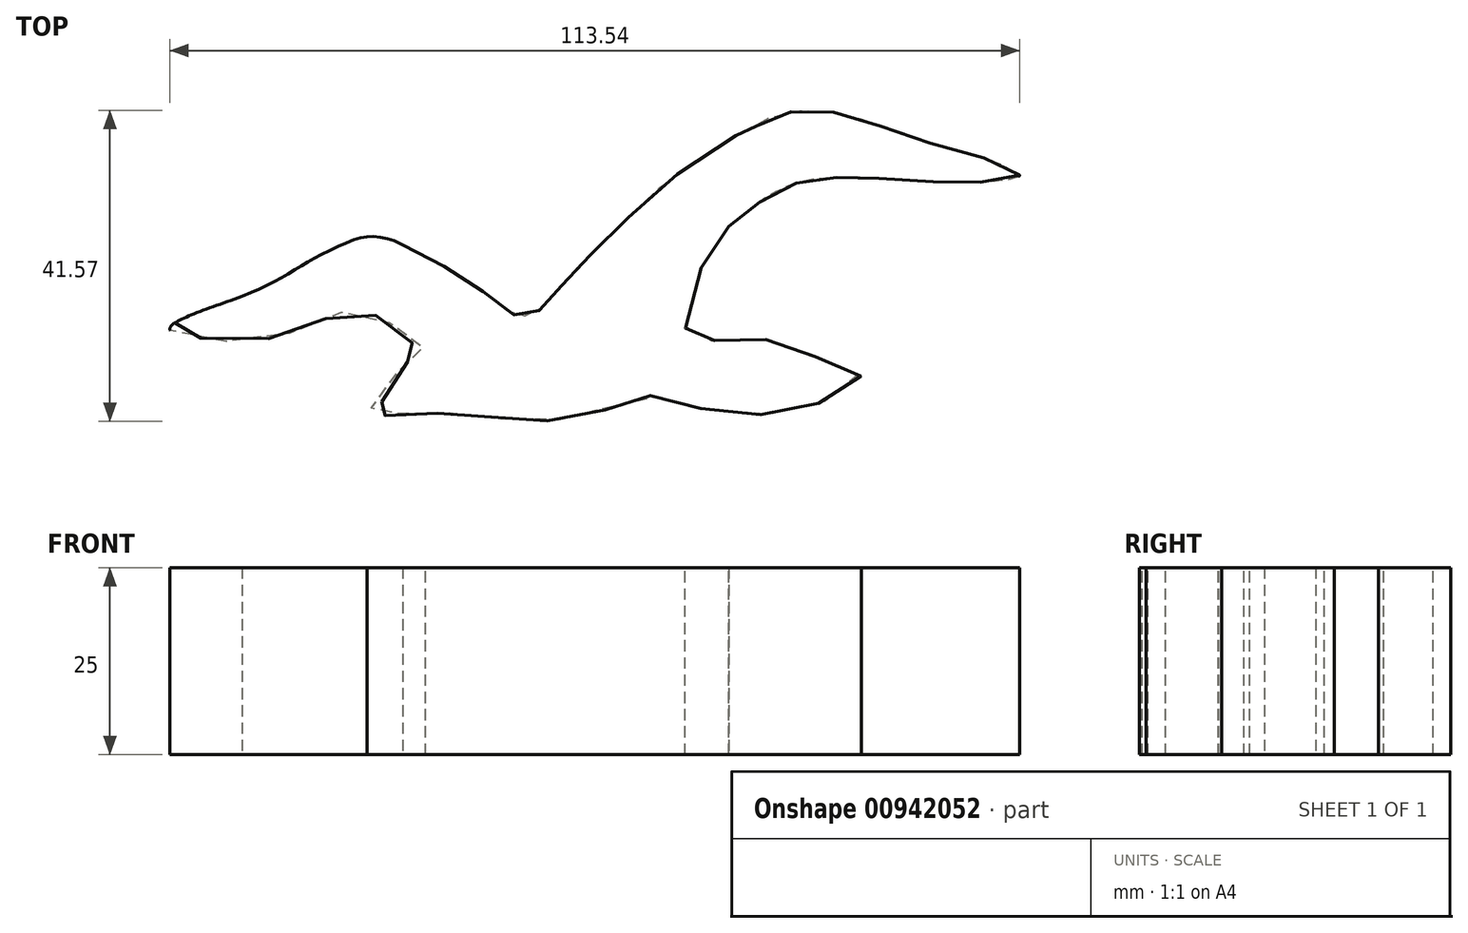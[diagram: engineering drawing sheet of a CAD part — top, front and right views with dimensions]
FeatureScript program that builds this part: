
annotation { "Feature Type Name" : "Feature", "Feature Type Description" : "" }
export const myFeature = defineFeature(function(context is Context, id is Id, definition is map)
    precondition{}
    {
        {
            var Q0;
            Q0=qCreatedBy(makeId("Top.planeOp"),FACE);
            var sketch = newSketch(context, id + "F0", { "sketchPlane" : qUnion([Q0])});
            skFitSpline(sketch, "E0", {"points": [v(-56.8, -12.41) * mm, v(-47.84, -8.9) * mm, v(-43.6, -6.97) * mm, v(-40.35, -5.11) * mm, v(-37.37, -3.4) * mm, v(-33.09, -1.42) * mm, v(-30.48, -0.9) * mm, v(-27.61, -1.42) * mm, v(-26.38, -2.02) * mm, v(-26.53, -2.1) * mm], "startDerivative": vector(50.93, 19.5) * mm, "endDerivative": vector(-17.67, -8.84) * mm});
            skFitSpline(sketch, "E1", {"points": [v(-26.38, -2.02) * mm, v(-21.97, -4.25) * mm, v(-16.88, -7.33) * mm, v(-14.1, -9.41) * mm, v(-11.23, -11.5) * mm, v(-10.2, -11.54) * mm, v(-8.2, -10.8) * mm, v(-6.98, -9.57) * mm, v(-4.36, -6.6) * mm, v(-1.68, -3.75) * mm, v(3.01, 0.89) * mm, v(10.34, 7.48) * mm, v(18.94, 13.1) * mm, v(19.68, 13.64) * mm, v(20.46, 13.64) * mm, v(22.1, 14.7) * mm, v(26.24, 15.86) * mm, v(30.42, 15.78) * mm, v(35.71, 14.5) * mm, v(41.56, 12.28) * mm, v(48.73, 10.37) * mm, v(54.54, 8.34) * mm, v(56.05, 7.23) * mm, v(52.6, 6.47) * mm, v(47.46, 6.35) * mm, v(40.93, 6.63) * mm, v(34.66, 6.98) * mm, v(31.1, 6.94) * mm, v(27.22, 6.47) * mm, v(23.1, 4.87) * mm, v(20.2, 2.8) * mm, v(17.19, 0.44) * mm], "startDerivative": vector(119.97, -57.7) * mm, "endDerivative": vector(-98.87, -76.43) * mm});
            skFitSpline(sketch, "E2", {"points": [v(17.19, 0.44) * mm, v(17.19, 0) * mm, v(15.2, -2.55) * mm, v(12.63, -6.86) * mm, v(11.41, -11.72) * mm, v(11.58, -14.81) * mm, v(11.74, -15.03) * mm, v(13.56, -14.87) * mm, v(18.2, -14.76) * mm, v(21.24, -14.6) * mm, v(23.06, -14.76) * mm, v(26.6, -15.75) * mm, v(29.85, -17.68) * mm, v(32.77, -19.12) * mm, v(34.92, -19.67) * mm, v(33.05, -21.38) * mm, v(29.02, -23.26) * mm, v(24.82, -24.3) * mm, v(20.52, -24.75) * mm, v(16.05, -24.36) * mm, v(11.63, -23.42) * mm, v(8.1, -22.48) * mm, v(6.11, -22.1) * mm, v(3.52, -22.87) * mm, v(0.54, -24.08) * mm, v(-3.32, -25.08) * mm, v(-8.02, -25.57) * mm, v(-12.6, -25.4) * mm, v(-17.4, -24.58) * mm, v(-19.27, -24.47) * mm, v(-22.25, -24.53) * mm, v(-25.51, -24.47) * mm, v(-28.99, -24.91) * mm, v(-31.03, -25.08) * mm, v(-30.64, -23.92) * mm, v(-28.71, -22.65) * mm, v(-28.05, -21.05) * mm, v(-25.79, -17.68) * mm, v(-23.47, -16.69) * mm, v(-23.47, -15.92) * mm, v(-25.01, -15.14) * mm, v(-27.11, -13.6) * mm, v(-28.71, -12) * mm, v(-32.24, -10.95) * mm, v(-35, -11.17) * mm, v(-38.43, -12.71) * mm, v(-42.84, -14.2) * mm, v(-47.92, -14.98) * mm, v(-54.05, -14.37) * mm, v(-57.3, -13.6) * mm, v(-57.47, -13.16) * mm, v(-56.8, -12.41) * mm, v(-47.84, -8.9) * mm], "startDerivative": vector(14.25, -51.42) * mm, "endDerivative": vector(332.45, 115.05) * mm});
            skSolve(sketch);
        }
        {
            var Q0;
            Q0 = qSketchRegion(id + "F0", true);
            extrude(context, id + "F1", {"entities" : qUnion([Q0]), "depth" : 25 * mm, "offsetDistance" : 25.4 * mm});
        }
    });
